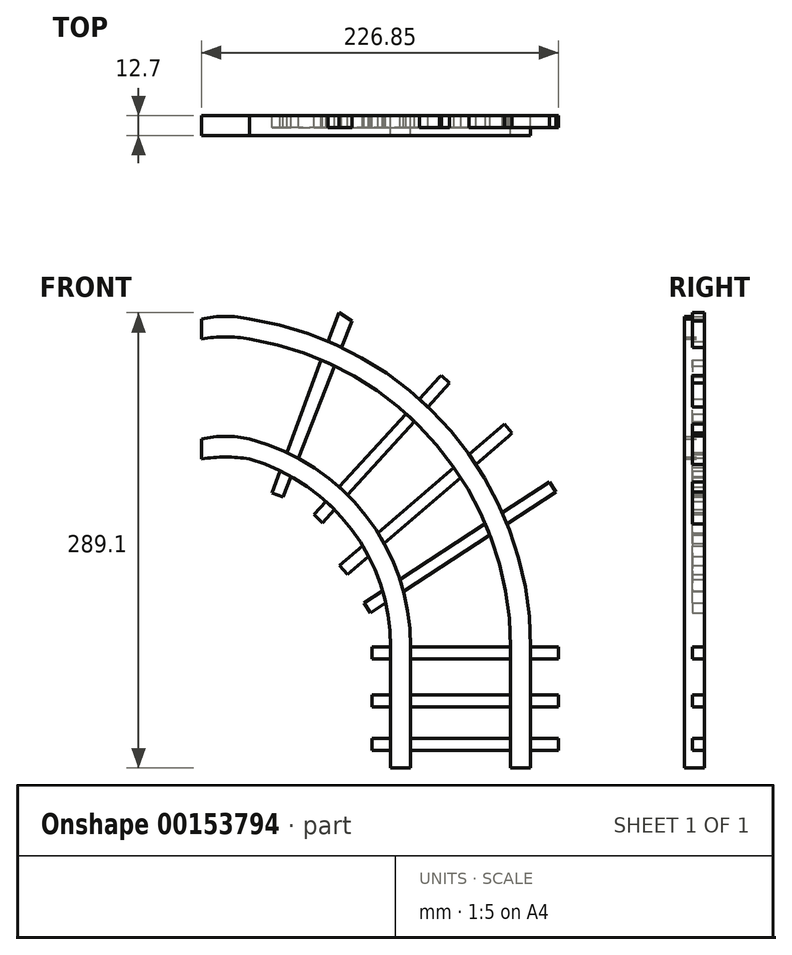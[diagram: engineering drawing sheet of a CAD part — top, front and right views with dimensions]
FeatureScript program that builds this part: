
annotation { "Feature Type Name" : "Feature", "Feature Type Description" : "" }
export const myFeature = defineFeature(function(context is Context, id is Id, definition is map)
    precondition{}
    {
        {
            var Q0;
            Q0=qCreatedBy(makeId("Front.planeOp"),FACE);
            var sketch = newSketch(context, id + "F0", { "sketchPlane" : qUnion([Q0])});
            skLineSegment(sketch, "E0", {"start": v(-53.95, 0) * mm, "end": v(-41.25, 0) * mm});
            skLineSegment(sketch, "E1", {"start": v(-41.25, 0) * mm, "end": v(-41.25, -76.88) * mm});
            skLineSegment(sketch, "E2", {"start": v(-53.95, 0) * mm, "end": v(-53.95, -76.88) * mm});
            skLineSegment(sketch, "E3", {"start": v(-53.95, -76.88) * mm, "end": v(-41.25, -76.88) * mm});
            skLineSegment(sketch, "E4", {"start": v(22.25, 0) * mm, "end": v(22.25, -76.88) * mm});
            skLineSegment(sketch, "E5", {"start": v(22.25, -76.88) * mm, "end": v(34.95, -76.88) * mm});
            skLineSegment(sketch, "E6", {"start": v(34.95, -76.88) * mm, "end": v(34.95, 0) * mm});
            skLineSegment(sketch, "E7", {"start": v(34.95, 0) * mm, "end": v(22.25, 0) * mm});
            skArc(sketch, "E8", {"start": v(-53.95, 0) * mm, "mid": v(-78.87, 74.61) * mm, "end": v(-143.62, 119.28) * mm});
            skArc(sketch, "E9", {"start": v(-41.25, 0) * mm, "mid": v(-69.84, 83.51) * mm, "end": v(-143.62, 131.98) * mm});
            skArc(sketch, "E10", {"start": v(22.25, 0) * mm, "mid": v(-24.8, 128.18) * mm, "end": v(-143.62, 195.48) * mm});
            skArc(sketch, "E11", {"start": v(34.95, 0) * mm, "mid": v(-15.8, 137.13) * mm, "end": v(-143.62, 208.18) * mm});
            skLineSegment(sketch, "E12", {"start": v(-65.9, -30.48) * mm, "end": v(-65.9, -38.1) * mm});
            skLineSegment(sketch, "E13", {"start": v(-65.9, -38.1) * mm, "end": v(52.75, -38.1) * mm});
            skLineSegment(sketch, "E14", {"start": v(52.75, -38.1) * mm, "end": v(52.75, -30.48) * mm});
            skLineSegment(sketch, "E15", {"start": v(52.75, -30.48) * mm, "end": v(-65.9, -30.48) * mm});
            skLineSegment(sketch, "E16", {"start": v(-65.9, 0) * mm, "end": v(-65.9, -7.62) * mm});
            skLineSegment(sketch, "E17", {"start": v(-65.9, -7.62) * mm, "end": v(52.75, -7.62) * mm});
            skLineSegment(sketch, "E18", {"start": v(52.75, -7.62) * mm, "end": v(52.75, 0) * mm});
            skLineSegment(sketch, "E19", {"start": v(52.75, 0) * mm, "end": v(-65.9, 0) * mm});
            skLineSegment(sketch, "E20", {"start": v(-78.51, 206.94) * mm, "end": v(-86.92, 212.22) * mm});
            skLineSegment(sketch, "E21", {"start": v(-86.92, 212.22) * mm, "end": v(-129.45, 97.84) * mm});
            skLineSegment(sketch, "E22", {"start": v(-129.45, 97.84) * mm, "end": v(-122.3, 95.18) * mm});
            skLineSegment(sketch, "E23", {"start": v(-122.3, 95.18) * mm, "end": v(-78.51, 206.94) * mm});
            skLineSegment(sketch, "E24", {"start": v(-81.4, 45.9) * mm, "end": v(-86.36, 51.68) * mm});
            skLineSegment(sketch, "E25", {"start": v(-86.36, 51.68) * mm, "end": v(18.3, 141.4) * mm});
            skLineSegment(sketch, "E26", {"start": v(21.2, 133.85) * mm, "end": v(-81.4, 45.9) * mm});
            skLineSegment(sketch, "E27", {"start": v(18.3, 141.4) * mm, "end": v(23.1, 135.8) * mm});
            skLineSegment(sketch, "E28", {"start": v(23.1, 135.8) * mm, "end": v(21.2, 133.85) * mm});
            skLineSegment(sketch, "E29", {"start": v(-70.95, 28) * mm, "end": v(46.88, 104.85) * mm});
            skLineSegment(sketch, "E30", {"start": v(46.88, 104.85) * mm, "end": v(51.04, 98.47) * mm});
            skLineSegment(sketch, "E31", {"start": v(51.04, 98.47) * mm, "end": v(-66.77, 21.62) * mm});
            skLineSegment(sketch, "E32", {"start": v(-70.95, 28) * mm, "end": v(-66.77, 21.62) * mm});
            skLineSegment(sketch, "E33", {"start": v(-102.62, 84.2) * mm, "end": v(-97.31, 78.74) * mm});
            skLineSegment(sketch, "E34", {"start": v(-102.62, 84.2) * mm, "end": v(-22.96, 171.29) * mm});
            skLineSegment(sketch, "E35", {"start": v(-97.31, 78.74) * mm, "end": v(-16.59, 167.68) * mm});
            skLineSegment(sketch, "E36", {"start": v(-16.59, 167.68) * mm, "end": v(-21.8, 172.46) * mm});
            skLineSegment(sketch, "E37", {"start": v(-21.8, 172.46) * mm, "end": v(-22.96, 171.29) * mm});
            skLineSegment(sketch, "E38", {"start": v(-65.9, -58.2) * mm, "end": v(-65.9, -65.83) * mm});
            skLineSegment(sketch, "E39", {"start": v(-65.9, -65.83) * mm, "end": v(52.75, -65.83) * mm});
            skLineSegment(sketch, "E40", {"start": v(52.75, -65.83) * mm, "end": v(52.75, -58.2) * mm});
            skLineSegment(sketch, "E41", {"start": v(52.75, -58.2) * mm, "end": v(-65.9, -58.2) * mm});
            skArc(sketch, "E42", {"start": v(-143.62, 208.18) * mm, "mid": v(-158.86, 209.93) * mm, "end": v(-174.1, 208.18) * mm});
            skArc(sketch, "E43", {"start": v(-143.62, 195.48) * mm, "mid": v(-158.86, 196.93) * mm, "end": v(-174.1, 195.48) * mm});
            skArc(sketch, "E44", {"start": v(-143.62, 131.98) * mm, "mid": v(-158.86, 133.74) * mm, "end": v(-174.1, 131.98) * mm});
            skArc(sketch, "E45", {"start": v(-143.62, 119.28) * mm, "mid": v(-158.86, 120.51) * mm, "end": v(-174.1, 119.28) * mm});
            skLineSegment(sketch, "E46", {"start": v(-174.1, 131.98) * mm, "end": v(-174.1, 119.28) * mm});
            skLineSegment(sketch, "E47", {"start": v(-174.1, 208.18) * mm, "end": v(-174.1, 195.48) * mm});
            skSolve(sketch);
        }
        {
            var Q0;
            {var subQ0=sQuery(id+"F0.wireOp",EDGE,"w6Ux8ujf-gO1w-YpWp-kq8u-cGSjs9h0iFOD");Q0=makeQuery(id+"F0.imprint","IMPRINT",FACE,{"disambiguationData":[TD([[makeQuery(id+"F0.imprint","IMPRINT",EDGE,{"derivedFrom":subQ0}),1.0]])]});}
            var Q1;
            {var subQ0=sQuery(id+"F0.wireOp",EDGE,"E23");var subQ1=sQuery(id+"F0.wireOp",EDGE,"E8");var subQ2=makeQuery(id+"F0.imprint","INTERSECT",VERTEX,{"derivedFrom":[subQ1,subQ0]});Q1=makeQuery(id+"F0.imprint","IMPRINT",FACE,{"disambiguationData":[TD([[makeQuery(id+"F0.imprint","IMPRINT",EDGE,{"disambiguationData":[TD([[subQ2,-1.0]])],"derivedFrom":subQ1}),-1.0]])]});}
            var Q2;
            {var subQ0=sQuery(id+"F0.wireOp",EDGE,"E34");var subQ1=sQuery(id+"F0.wireOp",EDGE,"E8");var subQ2=makeQuery(id+"F0.imprint","INTERSECT",VERTEX,{"derivedFrom":[subQ1,subQ0]});Q2=makeQuery(id+"F0.imprint","IMPRINT",FACE,{"disambiguationData":[TD([[makeQuery(id+"F0.imprint","IMPRINT",EDGE,{"disambiguationData":[TD([[subQ2,-1.0]])],"derivedFrom":subQ1}),-1.0]])]});}
            var Q3;
            {var subQ0=sQuery(id+"F0.wireOp",EDGE,"E35");var subQ1=sQuery(id+"F0.wireOp",EDGE,"E8");var subQ2=makeQuery(id+"F0.imprint","INTERSECT",VERTEX,{"derivedFrom":[subQ1,subQ0]});Q3=makeQuery(id+"F0.imprint","IMPRINT",FACE,{"disambiguationData":[TD([[makeQuery(id+"F0.imprint","IMPRINT",EDGE,{"disambiguationData":[TD([[subQ2,-1.0]])],"derivedFrom":subQ1}),-1.0]])]});}
            var Q4;
            {var subQ0=sQuery(id+"F0.wireOp",EDGE,"E25");var subQ1=sQuery(id+"F0.wireOp",EDGE,"E8");var subQ2=makeQuery(id+"F0.imprint","INTERSECT",VERTEX,{"derivedFrom":[subQ1,subQ0]});Q4=makeQuery(id+"F0.imprint","IMPRINT",FACE,{"disambiguationData":[TD([[makeQuery(id+"F0.imprint","IMPRINT",EDGE,{"disambiguationData":[TD([[subQ2,-1.0]])],"derivedFrom":subQ1}),-1.0]])]});}
            var Q5;
            {var subQ0=sQuery(id+"F0.wireOp",EDGE,"E26");var subQ1=sQuery(id+"F0.wireOp",EDGE,"E8");var subQ2=makeQuery(id+"F0.imprint","INTERSECT",VERTEX,{"derivedFrom":[subQ1,subQ0]});Q5=makeQuery(id+"F0.imprint","IMPRINT",FACE,{"disambiguationData":[TD([[makeQuery(id+"F0.imprint","IMPRINT",EDGE,{"disambiguationData":[TD([[subQ2,-1.0]])],"derivedFrom":subQ1}),-1.0]])]});}
            var Q6;
            {var subQ0=sQuery(id+"F0.wireOp",EDGE,"E29");var subQ1=sQuery(id+"F0.wireOp",EDGE,"E8");var subQ2=makeQuery(id+"F0.imprint","INTERSECT",VERTEX,{"derivedFrom":[subQ1,subQ0]});Q6=makeQuery(id+"F0.imprint","IMPRINT",FACE,{"disambiguationData":[TD([[makeQuery(id+"F0.imprint","IMPRINT",EDGE,{"disambiguationData":[TD([[subQ2,-1.0]])],"derivedFrom":subQ1}),-1.0]])]});}
            var Q7;
            {var subQ0=sQuery(id+"F0.wireOp",EDGE,"E31");var subQ1=sQuery(id+"F0.wireOp",EDGE,"E8");var subQ2=makeQuery(id+"F0.imprint","INTERSECT",VERTEX,{"derivedFrom":[subQ1,subQ0]});Q7=makeQuery(id+"F0.imprint","IMPRINT",FACE,{"disambiguationData":[TD([[makeQuery(id+"F0.imprint","IMPRINT",EDGE,{"disambiguationData":[TD([[subQ2,-1.0]])],"derivedFrom":subQ1}),-1.0]])]});}
            var Q8;
            {var subQ1=sQuery(id+"F0.wireOp",EDGE,"E8");var subQ3=sQuery(id+"F0.wireOp",EDGE,"E31");var subQ4=makeQuery(id+"F0.imprint","INTERSECT",VERTEX,{"derivedFrom":[subQ1,subQ3]});Q8=makeQuery(id+"F0.imprint","IMPRINT",FACE,{"disambiguationData":[TD([[makeQuery(id+"F0.imprint","IMPRINT",EDGE,{"disambiguationData":[TD([[subQ4,1.0]])],"derivedFrom":subQ3}),1.0]])]});}
            var Q9;
            {var subQ3=sQuery(id+"F0.wireOp",EDGE,"E17");var subQ5=sQuery(id+"F0.wireOp",EDGE,"E2");var subQ7=makeQuery(id+"F0.imprint","INTERSECT",VERTEX,{"derivedFrom":[subQ5,subQ3]});Q9=makeQuery(id+"F0.imprint","IMPRINT",FACE,{"disambiguationData":[TD([[makeQuery(id+"F0.imprint","IMPRINT",EDGE,{"disambiguationData":[TD([[subQ7,-1.0]])],"derivedFrom":subQ3}),1.0]])]});}
            var Q10;
            {var subQ0=sQuery(id+"F0.wireOp",EDGE,"E17");var subQ1=sQuery(id+"F0.wireOp",EDGE,"E1");var subQ2=makeQuery(id+"F0.imprint","INTERSECT",VERTEX,{"derivedFrom":[subQ1,subQ0]});Q10=makeQuery(id+"F0.imprint","IMPRINT",FACE,{"disambiguationData":[TD([[makeQuery(id+"F0.imprint","IMPRINT",EDGE,{"disambiguationData":[TD([[subQ2,-1.0]])],"derivedFrom":subQ1}),-1.0]])]});}
            var Q11;
            {var subQ0=sQuery(id+"F0.wireOp",EDGE,"E15");var subQ1=sQuery(id+"F0.wireOp",EDGE,"E1");var subQ2=makeQuery(id+"F0.imprint","INTERSECT",VERTEX,{"derivedFrom":[subQ1,subQ0]});Q11=makeQuery(id+"F0.imprint","IMPRINT",FACE,{"disambiguationData":[TD([[makeQuery(id+"F0.imprint","IMPRINT",EDGE,{"disambiguationData":[TD([[subQ2,-1.0]])],"derivedFrom":subQ1}),-1.0]])]});}
            var Q12;
            {var subQ0=sQuery(id+"F0.wireOp",EDGE,"E13");var subQ1=sQuery(id+"F0.wireOp",EDGE,"E1");var subQ2=makeQuery(id+"F0.imprint","INTERSECT",VERTEX,{"derivedFrom":[subQ1,subQ0]});Q12=makeQuery(id+"F0.imprint","IMPRINT",FACE,{"disambiguationData":[TD([[makeQuery(id+"F0.imprint","IMPRINT",EDGE,{"disambiguationData":[TD([[subQ2,-1.0]])],"derivedFrom":subQ1}),-1.0]])]});}
            var Q13;
            {var subQ0=sQuery(id+"F0.wireOp",EDGE,"E39");var subQ1=sQuery(id+"F0.wireOp",EDGE,"E1");var subQ2=makeQuery(id+"F0.imprint","INTERSECT",VERTEX,{"derivedFrom":[subQ1,subQ0]});Q13=makeQuery(id+"F0.imprint","IMPRINT",FACE,{"disambiguationData":[TD([[makeQuery(id+"F0.imprint","IMPRINT",EDGE,{"disambiguationData":[TD([[subQ2,1.0]])],"derivedFrom":subQ1}),-1.0]])]});}
            var Q14;
            {var subQ0=sQuery(id+"F0.wireOp",EDGE,"E3");Q14=makeQuery(id+"F0.imprint","IMPRINT",FACE,{"disambiguationData":[TD([[makeQuery(id+"F0.imprint","IMPRINT",EDGE,{"derivedFrom":subQ0}),1.0]])]});}
            var Q15;
            {var subQ0=sQuery(id+"F0.wireOp",EDGE,"E5");Q15=makeQuery(id+"F0.imprint","IMPRINT",FACE,{"disambiguationData":[TD([[makeQuery(id+"F0.imprint","IMPRINT",EDGE,{"derivedFrom":subQ0}),1.0]])]});}
            var Q16;
            {var subQ0=sQuery(id+"F0.wireOp",EDGE,"E39");var subQ1=sQuery(id+"F0.wireOp",EDGE,"E4");var subQ2=makeQuery(id+"F0.imprint","INTERSECT",VERTEX,{"derivedFrom":[subQ1,subQ0]});Q16=makeQuery(id+"F0.imprint","IMPRINT",FACE,{"disambiguationData":[TD([[makeQuery(id+"F0.imprint","IMPRINT",EDGE,{"disambiguationData":[TD([[subQ2,1.0]])],"derivedFrom":subQ1}),1.0]])]});}
            var Q17;
            {var subQ0=sQuery(id+"F0.wireOp",EDGE,"E13");var subQ1=sQuery(id+"F0.wireOp",EDGE,"E4");var subQ2=makeQuery(id+"F0.imprint","INTERSECT",VERTEX,{"derivedFrom":[subQ1,subQ0]});Q17=makeQuery(id+"F0.imprint","IMPRINT",FACE,{"disambiguationData":[TD([[makeQuery(id+"F0.imprint","IMPRINT",EDGE,{"disambiguationData":[TD([[subQ2,-1.0]])],"derivedFrom":subQ1}),1.0]])]});}
            var Q18;
            {var subQ0=sQuery(id+"F0.wireOp",EDGE,"E15");var subQ1=sQuery(id+"F0.wireOp",EDGE,"E4");var subQ2=makeQuery(id+"F0.imprint","INTERSECT",VERTEX,{"derivedFrom":[subQ1,subQ0]});Q18=makeQuery(id+"F0.imprint","IMPRINT",FACE,{"disambiguationData":[TD([[makeQuery(id+"F0.imprint","IMPRINT",EDGE,{"disambiguationData":[TD([[subQ2,-1.0]])],"derivedFrom":subQ1}),1.0]])]});}
            var Q19;
            {var subQ0=sQuery(id+"F0.wireOp",EDGE,"E17");var subQ1=sQuery(id+"F0.wireOp",EDGE,"E4");var subQ2=makeQuery(id+"F0.imprint","INTERSECT",VERTEX,{"derivedFrom":[subQ1,subQ0]});Q19=makeQuery(id+"F0.imprint","IMPRINT",FACE,{"disambiguationData":[TD([[makeQuery(id+"F0.imprint","IMPRINT",EDGE,{"disambiguationData":[TD([[subQ2,-1.0]])],"derivedFrom":subQ1}),1.0]])]});}
            var Q20;
            {var subQ3=sQuery(id+"F0.wireOp",EDGE,"E17");var subQ5=sQuery(id+"F0.wireOp",EDGE,"E6");var subQ7=makeQuery(id+"F0.imprint","INTERSECT",VERTEX,{"derivedFrom":[subQ5,subQ3]});Q20=makeQuery(id+"F0.imprint","IMPRINT",FACE,{"disambiguationData":[TD([[makeQuery(id+"F0.imprint","IMPRINT",EDGE,{"disambiguationData":[TD([[subQ7,1.0]])],"derivedFrom":subQ3}),1.0]])]});}
            var Q21;
            {var subQ3=sQuery(id+"F0.wireOp",EDGE,"E31");var subQ5=sQuery(id+"F0.wireOp",EDGE,"E11");var subQ6=makeQuery(id+"F0.imprint","INTERSECT",VERTEX,{"derivedFrom":[subQ5,subQ3]});Q21=makeQuery(id+"F0.imprint","IMPRINT",FACE,{"disambiguationData":[TD([[makeQuery(id+"F0.imprint","IMPRINT",EDGE,{"disambiguationData":[TD([[subQ6,-1.0]])],"derivedFrom":subQ3}),1.0]])]});}
            var Q22;
            {var subQ0=sQuery(id+"F0.wireOp",EDGE,"E31");var subQ1=sQuery(id+"F0.wireOp",EDGE,"E10");var subQ2=makeQuery(id+"F0.imprint","INTERSECT",VERTEX,{"derivedFrom":[subQ1,subQ0]});Q22=makeQuery(id+"F0.imprint","IMPRINT",FACE,{"disambiguationData":[TD([[makeQuery(id+"F0.imprint","IMPRINT",EDGE,{"disambiguationData":[TD([[subQ2,-1.0]])],"derivedFrom":subQ1}),-1.0]])]});}
            var Q23;
            {var subQ0=sQuery(id+"F0.wireOp",EDGE,"E29");var subQ1=sQuery(id+"F0.wireOp",EDGE,"E10");var subQ2=makeQuery(id+"F0.imprint","INTERSECT",VERTEX,{"derivedFrom":[subQ1,subQ0]});Q23=makeQuery(id+"F0.imprint","IMPRINT",FACE,{"disambiguationData":[TD([[makeQuery(id+"F0.imprint","IMPRINT",EDGE,{"disambiguationData":[TD([[subQ2,-1.0]])],"derivedFrom":subQ1}),-1.0]])]});}
            var Q24;
            {var subQ0=sQuery(id+"F0.wireOp",EDGE,"E26");var subQ1=sQuery(id+"F0.wireOp",EDGE,"E10");var subQ2=makeQuery(id+"F0.imprint","INTERSECT",VERTEX,{"derivedFrom":[subQ1,subQ0]});Q24=makeQuery(id+"F0.imprint","IMPRINT",FACE,{"disambiguationData":[TD([[makeQuery(id+"F0.imprint","IMPRINT",EDGE,{"disambiguationData":[TD([[subQ2,-1.0]])],"derivedFrom":subQ1}),-1.0]])]});}
            var Q25;
            {var subQ0=sQuery(id+"F0.wireOp",EDGE,"E25");var subQ1=sQuery(id+"F0.wireOp",EDGE,"E10");var subQ2=makeQuery(id+"F0.imprint","INTERSECT",VERTEX,{"derivedFrom":[subQ1,subQ0]});Q25=makeQuery(id+"F0.imprint","IMPRINT",FACE,{"disambiguationData":[TD([[makeQuery(id+"F0.imprint","IMPRINT",EDGE,{"disambiguationData":[TD([[subQ2,-1.0]])],"derivedFrom":subQ1}),-1.0]])]});}
            var Q26;
            {var subQ0=sQuery(id+"F0.wireOp",EDGE,"E35");var subQ1=sQuery(id+"F0.wireOp",EDGE,"E10");var subQ2=makeQuery(id+"F0.imprint","INTERSECT",VERTEX,{"derivedFrom":[subQ1,subQ0]});Q26=makeQuery(id+"F0.imprint","IMPRINT",FACE,{"disambiguationData":[TD([[makeQuery(id+"F0.imprint","IMPRINT",EDGE,{"disambiguationData":[TD([[subQ2,-1.0]])],"derivedFrom":subQ1}),-1.0]])]});}
            var Q27;
            {var subQ0=sQuery(id+"F0.wireOp",EDGE,"E34");var subQ1=sQuery(id+"F0.wireOp",EDGE,"E10");var subQ2=makeQuery(id+"F0.imprint","INTERSECT",VERTEX,{"derivedFrom":[subQ1,subQ0]});Q27=makeQuery(id+"F0.imprint","IMPRINT",FACE,{"disambiguationData":[TD([[makeQuery(id+"F0.imprint","IMPRINT",EDGE,{"disambiguationData":[TD([[subQ2,-1.0]])],"derivedFrom":subQ1}),-1.0]])]});}
            var Q28;
            {var subQ0=sQuery(id+"F0.wireOp",EDGE,"E21");var subQ1=sQuery(id+"F0.wireOp",EDGE,"E10");var subQ2=makeQuery(id+"F0.imprint","INTERSECT",VERTEX,{"derivedFrom":[subQ1,subQ0]});Q28=makeQuery(id+"F0.imprint","IMPRINT",FACE,{"disambiguationData":[TD([[makeQuery(id+"F0.imprint","IMPRINT",EDGE,{"disambiguationData":[TD([[subQ2,1.0]])],"derivedFrom":subQ1}),-1.0]])]});}
            var Q29;
            {var subQ0=sQuery(id+"F0.wireOp",EDGE,"I99X7zZT-2xmO-KFwr-K0kD-skip7Sm9oKD5");Q29=makeQuery(id+"F0.imprint","IMPRINT",FACE,{"disambiguationData":[TD([[makeQuery(id+"F0.imprint","IMPRINT",EDGE,{"derivedFrom":subQ0}),1.0]])]});}
            var Q30;
            {var subQ5=sQuery(id+"F0.wireOp",EDGE,"E42");Q30=makeQuery(id+"F0.imprint","IMPRINT",FACE,{"disambiguationData":[TD([[makeQuery(id+"F0.imprint","IMPRINT",EDGE,{"derivedFrom":subQ5}),1.0]])]});}
            var Q31;
            {var subQ5=sQuery(id+"F0.wireOp",EDGE,"E44");Q31=makeQuery(id+"F0.imprint","IMPRINT",FACE,{"disambiguationData":[TD([[makeQuery(id+"F0.imprint","IMPRINT",EDGE,{"derivedFrom":subQ5}),1.0]])]});}
            extrude(context, id + "F1", {"entities" : qUnion([Q0, Q1, Q2, Q3, Q4, Q5, Q6, Q7, Q8, Q9, Q10, Q11, Q12, Q13, Q14, Q15, Q16, Q17, Q18, Q19, Q20, Q21, Q22, Q23, Q24, Q25, Q26, Q27, Q28, Q29, Q30, Q31]), "depth" : 12.7 * mm});
        }
        {
            var Q0;
            {var subQ5=sQuery(id+"F0.wireOp",EDGE,"E22");Q0=makeQuery(id+"F0.imprint","IMPRINT",FACE,{"disambiguationData":[TD([[makeQuery(id+"F0.imprint","IMPRINT",EDGE,{"derivedFrom":subQ5}),1.0]])]});}
            var Q1;
            {var subQ0=sQuery(id+"F0.wireOp",EDGE,"E21");var subQ1=sQuery(id+"F0.wireOp",EDGE,"E9");var subQ2=makeQuery(id+"F0.imprint","INTERSECT",VERTEX,{"derivedFrom":[subQ1,subQ0]});Q1=makeQuery(id+"F0.imprint","IMPRINT",FACE,{"disambiguationData":[TD([[makeQuery(id+"F0.imprint","IMPRINT",EDGE,{"disambiguationData":[TD([[subQ2,1.0]])],"derivedFrom":subQ1}),-1.0]])]});}
            var Q2;
            {var subQ5=sQuery(id+"F0.wireOp",EDGE,"E20");Q2=makeQuery(id+"F0.imprint","IMPRINT",FACE,{"disambiguationData":[TD([[makeQuery(id+"F0.imprint","IMPRINT",EDGE,{"derivedFrom":subQ5}),1.0]])]});}
            var Q3;
            {var subQ0=sQuery(id+"F0.wireOp",EDGE,"E36");Q3=makeQuery(id+"F0.imprint","IMPRINT",FACE,{"disambiguationData":[TD([[makeQuery(id+"F0.imprint","IMPRINT",EDGE,{"derivedFrom":subQ0}),1.0]])]});}
            var Q4;
            {var subQ0=sQuery(id+"F0.wireOp",EDGE,"E35");var subQ1=sQuery(id+"F0.wireOp",EDGE,"E9");var subQ2=makeQuery(id+"F0.imprint","INTERSECT",VERTEX,{"derivedFrom":[subQ1,subQ0]});Q4=makeQuery(id+"F0.imprint","IMPRINT",FACE,{"disambiguationData":[TD([[makeQuery(id+"F0.imprint","IMPRINT",EDGE,{"disambiguationData":[TD([[subQ2,-1.0]])],"derivedFrom":subQ1}),-1.0]])]});}
            var Q5;
            {var subQ5=sQuery(id+"F0.wireOp",EDGE,"E33");Q5=makeQuery(id+"F0.imprint","IMPRINT",FACE,{"disambiguationData":[TD([[makeQuery(id+"F0.imprint","IMPRINT",EDGE,{"derivedFrom":subQ5}),1.0]])]});}
            var Q6;
            {var subQ5=sQuery(id+"F0.wireOp",EDGE,"E24");Q6=makeQuery(id+"F0.imprint","IMPRINT",FACE,{"disambiguationData":[TD([[makeQuery(id+"F0.imprint","IMPRINT",EDGE,{"derivedFrom":subQ5}),-1.0]])]});}
            var Q7;
            {var subQ0=sQuery(id+"F0.wireOp",EDGE,"E26");var subQ1=sQuery(id+"F0.wireOp",EDGE,"E9");var subQ2=makeQuery(id+"F0.imprint","INTERSECT",VERTEX,{"derivedFrom":[subQ1,subQ0]});Q7=makeQuery(id+"F0.imprint","IMPRINT",FACE,{"disambiguationData":[TD([[makeQuery(id+"F0.imprint","IMPRINT",EDGE,{"disambiguationData":[TD([[subQ2,-1.0]])],"derivedFrom":subQ1}),-1.0]])]});}
            var Q8;
            {var subQ4=sQuery(id+"F0.wireOp",EDGE,"E27");Q8=makeQuery(id+"F0.imprint","IMPRINT",FACE,{"disambiguationData":[TD([[makeQuery(id+"F0.imprint","IMPRINT",EDGE,{"derivedFrom":subQ4}),-1.0]])]});}
            var Q9;
            {var subQ5=sQuery(id+"F0.wireOp",EDGE,"E30");Q9=makeQuery(id+"F0.imprint","IMPRINT",FACE,{"disambiguationData":[TD([[makeQuery(id+"F0.imprint","IMPRINT",EDGE,{"derivedFrom":subQ5}),-1.0]])]});}
            var Q10;
            {var subQ0=sQuery(id+"F0.wireOp",EDGE,"E31");var subQ1=sQuery(id+"F0.wireOp",EDGE,"E9");var subQ2=makeQuery(id+"F0.imprint","INTERSECT",VERTEX,{"derivedFrom":[subQ1,subQ0]});Q10=makeQuery(id+"F0.imprint","IMPRINT",FACE,{"disambiguationData":[TD([[makeQuery(id+"F0.imprint","IMPRINT",EDGE,{"disambiguationData":[TD([[subQ2,-1.0]])],"derivedFrom":subQ1}),-1.0]])]});}
            var Q11;
            {var subQ5=sQuery(id+"F0.wireOp",EDGE,"E32");Q11=makeQuery(id+"F0.imprint","IMPRINT",FACE,{"disambiguationData":[TD([[makeQuery(id+"F0.imprint","IMPRINT",EDGE,{"derivedFrom":subQ5}),1.0]])]});}
            var Q12;
            {var subQ5=sQuery(id+"F0.wireOp",EDGE,"E16");Q12=makeQuery(id+"F0.imprint","IMPRINT",FACE,{"disambiguationData":[TD([[makeQuery(id+"F0.imprint","IMPRINT",EDGE,{"derivedFrom":subQ5}),1.0]])]});}
            var Q13;
            {var subQ5=sQuery(id+"F0.wireOp",EDGE,"E12");Q13=makeQuery(id+"F0.imprint","IMPRINT",FACE,{"disambiguationData":[TD([[makeQuery(id+"F0.imprint","IMPRINT",EDGE,{"derivedFrom":subQ5}),1.0]])]});}
            var Q14;
            {var subQ5=sQuery(id+"F0.wireOp",EDGE,"E38");Q14=makeQuery(id+"F0.imprint","IMPRINT",FACE,{"disambiguationData":[TD([[makeQuery(id+"F0.imprint","IMPRINT",EDGE,{"derivedFrom":subQ5}),1.0]])]});}
            var Q15;
            {var subQ0=sQuery(id+"F0.wireOp",EDGE,"E39");var subQ1=sQuery(id+"F0.wireOp",EDGE,"E1");var subQ2=makeQuery(id+"F0.imprint","INTERSECT",VERTEX,{"derivedFrom":[subQ1,subQ0]});Q15=makeQuery(id+"F0.imprint","IMPRINT",FACE,{"disambiguationData":[TD([[makeQuery(id+"F0.imprint","IMPRINT",EDGE,{"disambiguationData":[TD([[subQ2,1.0]])],"derivedFrom":subQ1}),1.0]])]});}
            var Q16;
            {var subQ0=sQuery(id+"F0.wireOp",EDGE,"E15");var subQ1=sQuery(id+"F0.wireOp",EDGE,"E1");var subQ2=makeQuery(id+"F0.imprint","INTERSECT",VERTEX,{"derivedFrom":[subQ1,subQ0]});Q16=makeQuery(id+"F0.imprint","IMPRINT",FACE,{"disambiguationData":[TD([[makeQuery(id+"F0.imprint","IMPRINT",EDGE,{"disambiguationData":[TD([[subQ2,-1.0]])],"derivedFrom":subQ1}),1.0]])]});}
            var Q17;
            {var subQ1=sQuery(id+"F0.wireOp",EDGE,"E1");var subQ3=sQuery(id+"F0.wireOp",EDGE,"E17");var subQ4=makeQuery(id+"F0.imprint","INTERSECT",VERTEX,{"derivedFrom":[subQ1,subQ3]});Q17=makeQuery(id+"F0.imprint","IMPRINT",FACE,{"disambiguationData":[TD([[makeQuery(id+"F0.imprint","IMPRINT",EDGE,{"disambiguationData":[TD([[subQ4,-1.0]])],"derivedFrom":subQ3}),1.0]])]});}
            var Q18;
            {var subQ5=sQuery(id+"F0.wireOp",EDGE,"E18");Q18=makeQuery(id+"F0.imprint","IMPRINT",FACE,{"disambiguationData":[TD([[makeQuery(id+"F0.imprint","IMPRINT",EDGE,{"derivedFrom":subQ5}),1.0]])]});}
            var Q19;
            {var subQ5=sQuery(id+"F0.wireOp",EDGE,"E14");Q19=makeQuery(id+"F0.imprint","IMPRINT",FACE,{"disambiguationData":[TD([[makeQuery(id+"F0.imprint","IMPRINT",EDGE,{"derivedFrom":subQ5}),1.0]])]});}
            var Q20;
            {var subQ5=sQuery(id+"F0.wireOp",EDGE,"E40");Q20=makeQuery(id+"F0.imprint","IMPRINT",FACE,{"disambiguationData":[TD([[makeQuery(id+"F0.imprint","IMPRINT",EDGE,{"derivedFrom":subQ5}),1.0]])]});}
            extrude(context, id + "F2", {"entities" : qUnion([Q0, Q1, Q2, Q3, Q4, Q5, Q6, Q7, Q8, Q9, Q10, Q11, Q12, Q13, Q14, Q15, Q16, Q17, Q18, Q19, Q20]), "depth" : 7.62 * mm});
        }
    });
